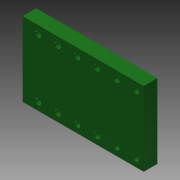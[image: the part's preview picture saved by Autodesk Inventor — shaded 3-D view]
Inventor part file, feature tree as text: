
AUTODESK INVENTOR PART (.ipt)
format: ipt  version: 2013 (Build 170138000, 138)  size: 104,960 bytes
history: native  units: mm
features: other x1, extrude x1, sketch x1
ambient origin geometry x8: Origin, YZ Plane, XZ Plane, XY Plane, X Axis, Y Axis, Z Axis, Center Point
feature tree (3):
  other  "ソリッド1"
  extrude  "押し出し1"  Depth=62.0mm
  sketch  "スケッチ1"
